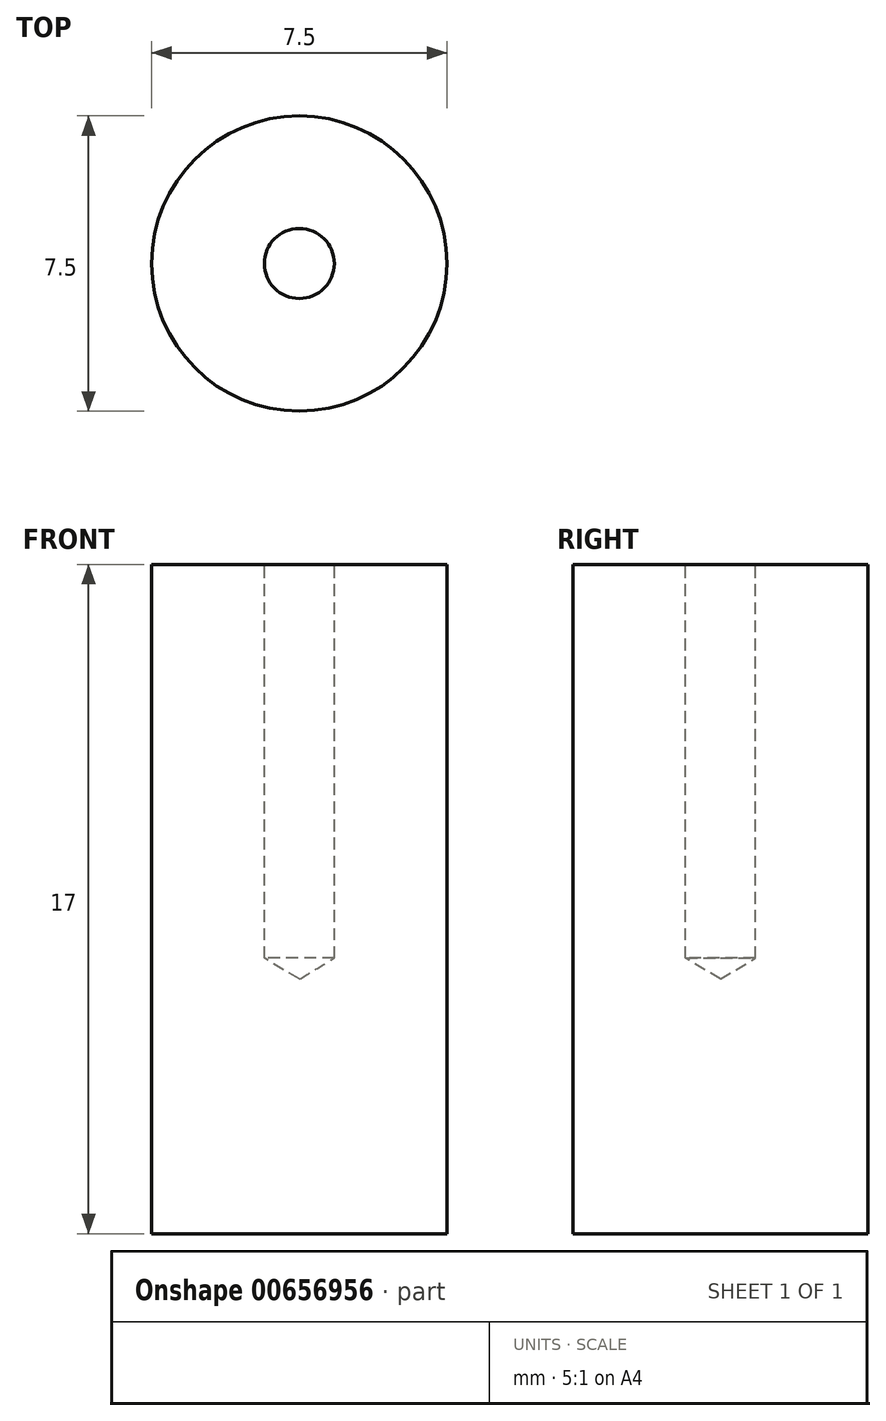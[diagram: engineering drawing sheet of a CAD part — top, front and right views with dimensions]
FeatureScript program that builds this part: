
annotation { "Feature Type Name" : "Feature", "Feature Type Description" : "" }
export const myFeature = defineFeature(function(context is Context, id is Id, definition is map)
    precondition{}
    {
        {
            assignVariable(context, id + "F0", {"name" : "length", "anyValue" : 17});
        }
        {
            var Q0;
            Q0=qCreatedBy(makeId("Top.planeOp"),FACE);
            var sketch = newSketch(context, id + "F1", { "sketchPlane" : qUnion([Q0])});
            skCircle(sketch, "E0", {"center": v(0, 0) * mm, "radius": 3.75 * mm});
            skSolve(sketch);
        }
        {
            var Q0;
            Q0=makeQuery(id+"F1.imprint","IMPRINT",FACE,{"disambiguationData":[TD([[makeQuery(id+"F1.imprint","IMPRINT",EDGE,{"derivedFrom":sQuery(id+"F1.wireOp",EDGE,"E0")}),1.0]])]});
            extrude(context, id + "F2", {"entities" : qUnion([Q0]), "depth" : (getVariable(context, 'length')) * mm, "offsetDistance" : 25 * mm});
        }
        {
            var Q0;
            Q0=makeQuery(id+"F2.opExtrude","CAP_FACE",FACE,{"disambiguationData":[OSD([sQuery(id+"F1.wireOp",EDGE,"E0")])],"isStart":false});
            var sketch = newSketch(context, id + "F3", { "sketchPlane" : qUnion([Q0])});
            skPoint(sketch, "E1", {"position": v(0, 0) * mm});
            skSolve(sketch);
        }
        {
            var Q0;
            Q0=sQuery(id+"F3.wireOp",VERTEX,"E1");
            var Q1;
            Q1=makeQuery(id+"F2.opExtrude","SWEPT_BODY",BODY,{"disambiguationData":[OSD([sQuery(id+"F1.wireOp",EDGE,"E0")])]});
            hole(context, id + "F4", {"style" : HoleStyle.SIMPLE, "endStyle" : HoleEndStyle.BLIND, "standardTappedOrClearance" : lookupTablePath({ "standard" : "ANSI", "engagement" : "75%", "pitch" : "56 tpi", "size" : "#2", "type" : "Tapped" }), "standardBlindInLast" : lookupTablePath({ "standard" : "ANSI", "engagement" : "75%", "pitch" : "56 tpi", "size" : "#2", "type" : "Tapped" }), "holeDiameter" : 1.78 * mm, "majorDiameter" : 2.18 * mm, "showTappedDepth" : true, "holeDepth" : 10 * mm, "isTappedThrough" : true, "tappedDepth" : 10 * mm, "tapClearance" : 0, "startFromSketch" : true, "locations" : qUnion([Q0]), "scope" : qUnion([Q1])});
        }
    });
